# Revit family: 05L
name_source: partatom
category: Lighting Fixtures
revit_build: Autodesk Revit 2014 (Build: 20130308_1515(x64)
units: mm (PartAtom-declared; Revit-internal decimal feet)

## types (2) — shared parameters
Apparent Load = 36 VA
Assembly Code = D5020200
Color Filter = 16777215
Connector Description = Lighting Connector
Default Elevation = 1219.2 mm  [stored 4 ft]
Description = The next generation in LED linear luminaires, the Protecta X’s
revolutionary design puts LED at the centre to provide the
performance of a 4ft linear in a lightweight and slimline package.
With a robust enclosure and excellent IP, the Protecta X is suitable
for use in the world’s most arduous environments. Expected useful
life to 70% of the initial lumens (L70) is >200,000 hours at 25°C,
with an incredible 90,000 maintenance free hours at 60°C. For a
luminaire with the longest life, the highest output and marketleading efficacy, choose the Protecta X
Dimming Lamp Color Temperature Shift = <None>
Drum-Height = 609.6 mm  [stored 2 ft]
Emit Shape Visible in Rendering = No
Emit from Rectangle Length = 314 mm  [stored 1.03018 ft]
Emit from Rectangle Width = 504 mm  [stored 1.65354 ft]
Features = 120,000-hour maintenance free lifespan at 25 degC
> 90,000 maintenance free hours at 60 degC
The lumen output of a 4ft linear in a lightweight and slimline package using specialised optics
A targeted bright, white output with minimal spill light
Market-leading efficacy of = 135 lm/W
Up to 50% energy savings vs traditional fluorescent fixtures
Multiple beam distributions available
Fixture distribution = Direct
Housing Material = Paint - Hubbell - Matte White
Lamp = LED
Length = 504 mm  [stored 1.65354 ft]
Load Classification = Lighting
Manufacturer = Chalmit
Power Factor = 1
Product Documentation Link = https://hubbellcdn.com
Product Link = https://www.hubbell.com
Reflector Finish = Hubbell - White Glass
Tilt Angle = 90.00°
URL = https://www.hubbell.com
Voltage = 120 V
Warranty = 5 years Warranty
Wattage Comments = 36W
Watts = 36 W
Width = 314 mm  [stored 1.03018 ft]
Wings = Paint - Hubbell - Light Silver

## per-type parameters (varying)
| type | Photometric Web File |
| PRXB/05L/LE | PRXB_05L_LE.ies |
| PRXB/05L/LE/EM | PRXB_05L_LE_EM.ies |

note: column(s) folded — value = type name in every type: Model

note: [stored X ft] marks values corroborated as IEEE doubles in the binary element streams (Revit-internal decimal feet)

## geometry (parser evidence)
native form markers: Sweep x6
no freeform markers — native parametric forms only
